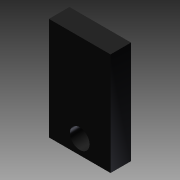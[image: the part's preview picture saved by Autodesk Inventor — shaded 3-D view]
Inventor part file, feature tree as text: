
AUTODESK INVENTOR PART (.ipt)
format: ipt  version: 2012 (Build 160160000, 160)  size: 87,552 bytes
history: native  units: in
note: dims shown in document units (in); Inventor stores cm internally (conversion verified against a paired STEP export)
features: hole x3, sketch x3, extrude x1
ambient origin geometry x8: Origin, YZ Plane, XZ Plane, XY Plane, X Axis, Y Axis, Z Axis, Center Point
bodies: Solid1 (feature_tree)
feature tree (7):
  extrude  "Extrusion1"  Depth=0.5in
  hole  "Hole1"  [1 undecoded]
  hole  "Hole3"  [1 undecoded]
  sketch  "Sketch1"  dims[d0=0.3in d1=0.5in]
  sketch  "Sketch2"  dims[d2=0.1in d3=0.0in d4=0.15in]
  sketch  "Sketch3"  dims[d5=0.07in d6=0.096in d7=0.75in d8=0.172in d9=0.25in d10=0.5635in d11=0.2055in d12=0.8108in d13=0.13in d14=0.457in d15=0.375in d16=0.25in d17=0.5635in d18=0.539in d19=120.0deg]
  hole  "Hole2"  [1 undecoded]
note: 3 required parameter values undecoded (feature->parameter linkage not recoverable at this tier; creation-order binding heuristic only, values carry confidence <= 0.55)
